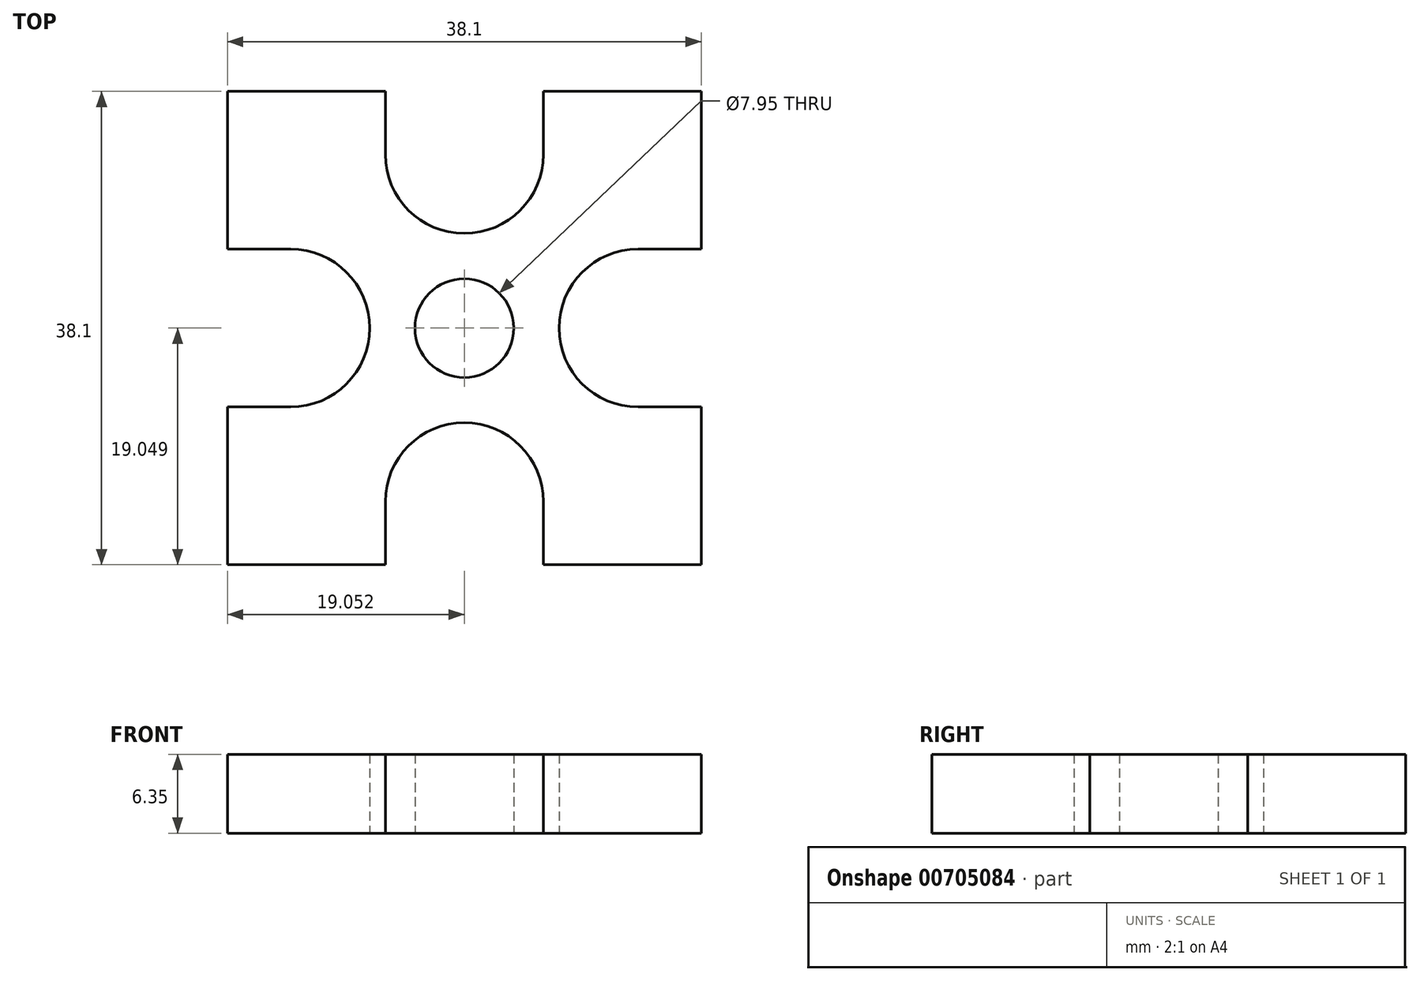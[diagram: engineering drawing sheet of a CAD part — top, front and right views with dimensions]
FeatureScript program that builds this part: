
annotation { "Feature Type Name" : "Feature", "Feature Type Description" : "" }
export const myFeature = defineFeature(function(context is Context, id is Id, definition is map)
    precondition{}
    {
        {
            var Q0;
            Q0=qCreatedBy(makeId("Top.planeOp"),FACE);
            var sketch = newSketch(context, id + "F0", { "sketchPlane" : qUnion([Q0])});
            skCircle(sketch, "E0", {"center": v(19.05, 19.05) * mm, "radius": 3.98 * mm});
            skLineSegment(sketch, "E1", {"start": v(12.7, 5.08) * mm, "end": v(12.7, 0) * mm});
            skLineSegment(sketch, "E2", {"start": v(25.4, 5.08) * mm, "end": v(25.4, 0) * mm});
            skArc(sketch, "E3.trimOffspring", {"start": v(25.4, 5.08) * mm, "mid": v(19.05, 11.43) * mm, "end": v(12.7, 5.08) * mm});
            skArc(sketch, "E4.1.0", {"start": v(33.02, 25.4) * mm, "mid": v(26.67, 19.05) * mm, "end": v(33.02, 12.7) * mm});
            skLineSegment(sketch, "E4.1.1", {"start": v(33.02, 12.7) * mm, "end": v(38.1, 12.7) * mm});
            skLineSegment(sketch, "E4.1.2", {"start": v(33.02, 25.4) * mm, "end": v(38.1, 25.4) * mm});
            skArc(sketch, "E4.2.0", {"start": v(12.7, 33.02) * mm, "mid": v(19.05, 26.67) * mm, "end": v(25.4, 33.02) * mm});
            skLineSegment(sketch, "E4.2.1", {"start": v(25.4, 33.02) * mm, "end": v(25.4, 38.1) * mm});
            skLineSegment(sketch, "E4.2.2", {"start": v(12.7, 33.02) * mm, "end": v(12.7, 38.1) * mm});
            skArc(sketch, "E4.3.0", {"start": v(5.08, 12.7) * mm, "mid": v(11.43, 19.05) * mm, "end": v(5.08, 25.4) * mm});
            skLineSegment(sketch, "E4.3.1", {"start": v(5.08, 25.4) * mm, "end": v(0, 25.4) * mm});
            skLineSegment(sketch, "E4.3.2", {"start": v(5.08, 12.7) * mm, "end": v(0, 12.7) * mm});
            skLineSegment(sketch, "E5", {"start": v(0, 0) * mm, "end": v(0, 12.7) * mm});
            skLineSegment(sketch, "E6", {"start": v(0, 25.4) * mm, "end": v(0, 38.1) * mm});
            skLineSegment(sketch, "E7", {"start": v(0, 38.1) * mm, "end": v(12.7, 38.1) * mm});
            skLineSegment(sketch, "E8", {"start": v(25.4, 38.1) * mm, "end": v(38.1, 38.1) * mm});
            skLineSegment(sketch, "E9", {"start": v(38.1, 25.4) * mm, "end": v(38.1, 38.1) * mm});
            skLineSegment(sketch, "E10", {"start": v(0, 0) * mm, "end": v(12.7, 0) * mm});
            skLineSegment(sketch, "E11", {"start": v(25.4, 0) * mm, "end": v(38.1, 0) * mm});
            skLineSegment(sketch, "E12", {"start": v(38.1, 0) * mm, "end": v(38.1, 12.7) * mm});
            skSolve(sketch);
        }
        {
            var Q0;
            Q0=makeQuery(id+"F0.imprint","IMPRINT",FACE,{"disambiguationData":[TD([[makeQuery(id+"F0.imprint","IMPRINT",EDGE,{"derivedFrom":sQuery(id+"F0.wireOp",EDGE,"E0")}),-1.0]])]});
            extrude(context, id + "F1", {"entities" : qUnion([Q0]), "depth" : 6.35 * mm, "offsetDistance" : 25.4 * mm});
        }
    });
